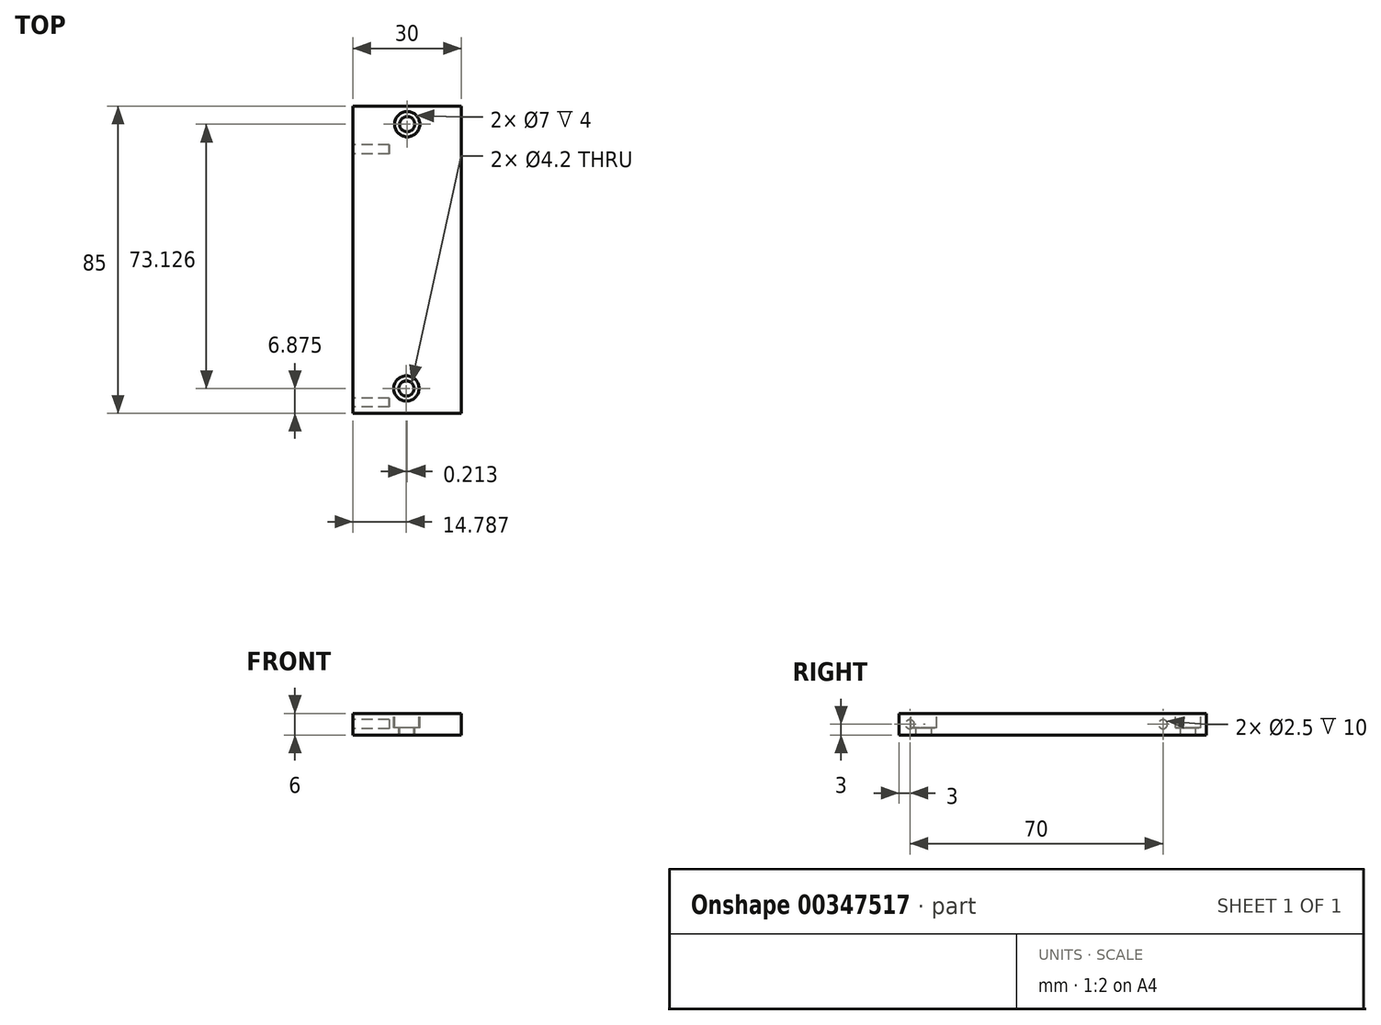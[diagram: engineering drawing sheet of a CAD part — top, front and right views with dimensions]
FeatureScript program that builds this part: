
annotation { "Feature Type Name" : "Feature", "Feature Type Description" : "" }
export const myFeature = defineFeature(function(context is Context, id is Id, definition is map)
    precondition{}
    {
        {
            var Q0;
            Q0=qCreatedBy(makeId("Top.planeOp"),FACE);
            var sketch = newSketch(context, id + "F0", { "sketchPlane" : qUnion([Q0])});
            skLineSegment(sketch, "E0.bottom", {"start": v(0, 0) * mm, "end": v(30, 0) * mm});
            skLineSegment(sketch, "E0.top", {"start": v(0, 85) * mm, "end": v(30, 85) * mm});
            skLineSegment(sketch, "E0.left", {"start": v(0, 0) * mm, "end": v(0, 85) * mm});
            skLineSegment(sketch, "E0.right", {"start": v(30, 0) * mm, "end": v(30, 85) * mm});
            skSolve(sketch);
        }
        {
            var Q0;
            Q0=makeQuery(id+"F0.imprint","IMPRINT",FACE,{"disambiguationData":[TD([[makeQuery(id+"F0.imprint","IMPRINT",EDGE,{"derivedFrom":sQuery(id+"F0.wireOp",EDGE,"E0.bottom")}),1.0]])]});
            extrude(context, id + "F1", {"entities" : qUnion([Q0]), "depth" : 6 * mm});
        }
        {
            var Q0;
            Q0=makeQuery(id+"F1.opExtrude","CAP_FACE",FACE,{"disambiguationData":[OSD([sQuery(id+"F0.wireOp",EDGE,"E0.bottom"),sQuery(id+"F0.wireOp",EDGE,"E0.top"),sQuery(id+"F0.wireOp",EDGE,"E0.left"),sQuery(id+"F0.wireOp",EDGE,"E0.right")])],"isStart":false});
            var sketch = newSketch(context, id + "F2", { "sketchPlane" : qUnion([Q0])});
            skCircle(sketch, "E1", {"center": v(15, 80) * mm, "radius": 3.5 * mm});
            skSolve(sketch);
        }
        {
            var Q0;
            Q0=makeQuery(id+"F2.imprint","IMPRINT",FACE,{"disambiguationData":[TD([[makeQuery(id+"F2.imprint","IMPRINT",EDGE,{"derivedFrom":sQuery(id+"F2.wireOp",EDGE,"E1")}),1.0]])]});
            var Q1;
            Q1=sQuery(id+"F2.wireOp",EDGE,"E1");
            extrude(context, id + "F3", {"entities" : qUnion([Q0]), "operationType" : NewBodyOperationType.REMOVE, "surfaceEntities" : qUnion([Q1]), "oppositeDirection" : true, "depth" : 4 * mm});
        }
        {
            var Q0;
            Q0=makeQuery(id+"F3.boolean.opBoolean","COPY",FACE,{"derivedFrom":makeQuery(id+"F3.opExtrude","CAP_FACE",FACE,{"disambiguationData":[OSD([sQuery(id+"F2.wireOp",EDGE,"E1")])],"isStart":false})});
            var sketch = newSketch(context, id + "F4", { "sketchPlane" : qUnion([Q0])});
            skCircle(sketch, "E2", {"center": v(15, 80) * mm, "radius": 2.1 * mm});
            skSolve(sketch);
        }
        {
            var Q0;
            Q0=makeQuery(id+"F4.imprint","IMPRINT",FACE,{"disambiguationData":[TD([[makeQuery(id+"F4.imprint","IMPRINT",EDGE,{"derivedFrom":sQuery(id+"F4.wireOp",EDGE,"E2")}),1.0]])]});
            var Q1;
            Q1=sQuery(id+"F4.wireOp",EDGE,"E2");
            extrude(context, id + "F5", {"entities" : qUnion([Q0]), "operationType" : NewBodyOperationType.REMOVE, "surfaceEntities" : qUnion([Q1]), "oppositeDirection" : true, "depth" : 25 * mm});
        }
        {
            var Q0;
            Q0=makeQuery(id+"F1.opExtrude","CAP_FACE",FACE,{"disambiguationData":[OSD([sQuery(id+"F0.wireOp",EDGE,"E0.bottom"),sQuery(id+"F0.wireOp",EDGE,"E0.top"),sQuery(id+"F0.wireOp",EDGE,"E0.left"),sQuery(id+"F0.wireOp",EDGE,"E0.right")])],"isStart":false});
            var sketch = newSketch(context, id + "F6", { "sketchPlane" : qUnion([Q0])});
            skCircle(sketch, "E3", {"center": v(14.79, 6.87) * mm, "radius": 3.5 * mm});
            skSolve(sketch);
        }
        {
            var Q0;
            Q0=makeQuery(id+"F6.imprint","IMPRINT",FACE,{"disambiguationData":[TD([[makeQuery(id+"F6.imprint","IMPRINT",EDGE,{"derivedFrom":sQuery(id+"F6.wireOp",EDGE,"E3")}),1.0]])]});
            var Q1;
            Q1=sQuery(id+"F6.wireOp",EDGE,"E3");
            extrude(context, id + "F7", {"entities" : qUnion([Q0]), "operationType" : NewBodyOperationType.REMOVE, "surfaceEntities" : qUnion([Q1]), "oppositeDirection" : true, "depth" : 4 * mm});
        }
        {
            var Q0;
            Q0=makeQuery(id+"F7.boolean.opBoolean","COPY",FACE,{"derivedFrom":makeQuery(id+"F7.opExtrude","CAP_FACE",FACE,{"disambiguationData":[OSD([sQuery(id+"F6.wireOp",EDGE,"E3")])],"isStart":false})});
            var sketch = newSketch(context, id + "F8", { "sketchPlane" : qUnion([Q0])});
            skCircle(sketch, "E4", {"center": v(14.79, 6.87) * mm, "radius": 2.1 * mm});
            skSolve(sketch);
        }
        {
            var Q0;
            Q0=makeQuery(id+"F8.imprint","IMPRINT",FACE,{"disambiguationData":[TD([[makeQuery(id+"F8.imprint","IMPRINT",EDGE,{"derivedFrom":sQuery(id+"F8.wireOp",EDGE,"E4")}),1.0]])]});
            var Q1;
            Q1=sQuery(id+"F8.wireOp",EDGE,"E4");
            extrude(context, id + "F9", {"entities" : qUnion([Q0]), "operationType" : NewBodyOperationType.REMOVE, "surfaceEntities" : qUnion([Q1]), "oppositeDirection" : true, "depth" : 25 * mm});
        }
        {
            var Q0;
            Q0=makeQuery(id+"F1.opExtrude","SWEPT_FACE",FACE,{"disambiguationData":[OSD([sQuery(id+"F0.wireOp",EDGE,"E0.left")])]});
            var sketch = newSketch(context, id + "F10", { "sketchPlane" : qUnion([Q0])});
            skCircle(sketch, "E5", {"center": v(-3, 3) * mm, "radius": 1.25 * mm});
            skSolve(sketch);
        }
        {
            var Q0;
            Q0=makeQuery(id+"F10.imprint","IMPRINT",FACE,{"disambiguationData":[TD([[makeQuery(id+"F10.imprint","IMPRINT",EDGE,{"derivedFrom":sQuery(id+"F10.wireOp",EDGE,"E5")}),-1.0]])]});
            var sketch = newSketch(context, id + "F11", { "sketchPlane" : qUnion([Q0])});
            skCircle(sketch, "E6", {"center": v(-73, 3) * mm, "radius": 1.25 * mm});
            skSolve(sketch);
        }
        {
            var Q0;
            Q0 = qSketchRegion(id + "F11", true);
            extrude(context, id + "F12", {"entities" : qUnion([Q0]), "operationType" : NewBodyOperationType.REMOVE, "oppositeDirection" : true, "depth" : 10 * mm});
        }
        {
            var Q0;
            Q0=makeQuery(id+"F10.imprint","IMPRINT",FACE,{"disambiguationData":[TD([[makeQuery(id+"F10.imprint","IMPRINT",EDGE,{"derivedFrom":sQuery(id+"F10.wireOp",EDGE,"E5")}),1.0]])]});
            var Q1;
            Q1=sQuery(id+"F10.wireOp",EDGE,"E5");
            extrude(context, id + "F13", {"entities" : qUnion([Q0]), "operationType" : NewBodyOperationType.REMOVE, "surfaceEntities" : qUnion([Q1]), "oppositeDirection" : true, "depth" : 10 * mm});
        }
    });
